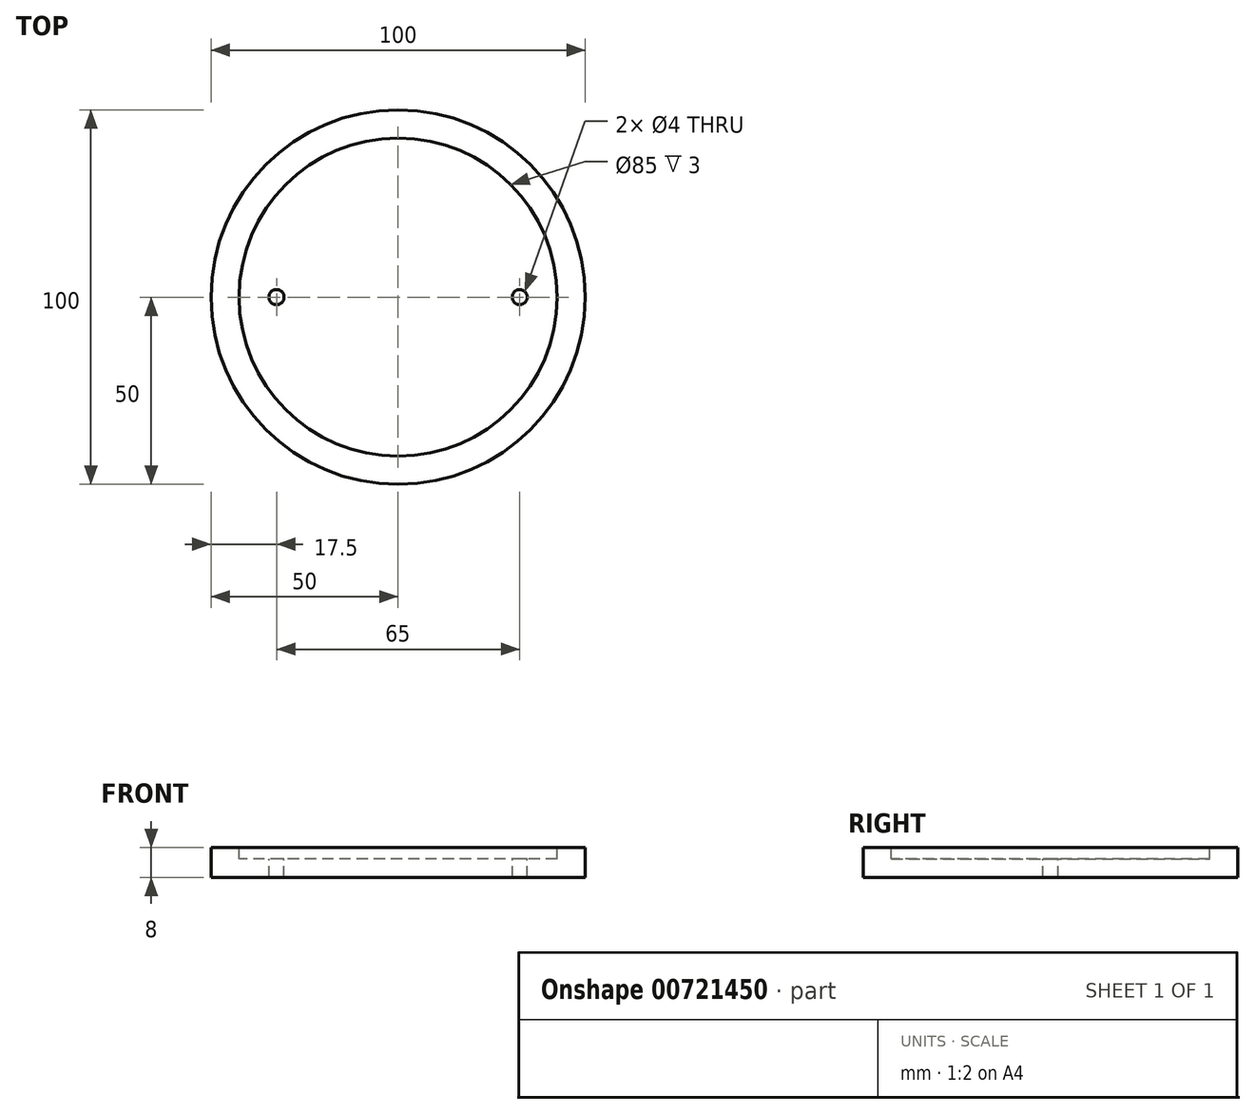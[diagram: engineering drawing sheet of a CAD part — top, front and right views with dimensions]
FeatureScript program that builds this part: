
annotation { "Feature Type Name" : "Feature", "Feature Type Description" : "" }
export const myFeature = defineFeature(function(context is Context, id is Id, definition is map)
    precondition{}
    {
        {
            var Q0;
            Q0=qCreatedBy(makeId("Top.planeOp"),FACE);
            var sketch = newSketch(context, id + "F0", { "sketchPlane" : qUnion([Q0])});
            skCircle(sketch, "E0", {"center": v(0, 0) * mm, "radius": 50 * mm});
            skSolve(sketch);
        }
        {
            var Q0;
            Q0 = qSketchRegion(id + "F0", true);
            extrude(context, id + "F1", {"entities" : qUnion([Q0]), "depth" : 8 * mm, "offsetDistance" : 25 * mm});
        }
        {
            var Q0;
            Q0=makeQuery(id+"F1.opExtrude","CAP_FACE",FACE,{"disambiguationData":[OSD([sQuery(id+"F0.wireOp",EDGE,"E0")])],"isStart":false});
            var sketch = newSketch(context, id + "F2", { "sketchPlane" : qUnion([Q0])});
            skCircle(sketch, "E1", {"center": v(0, 0) * mm, "radius": 42.5 * mm});
            skSolve(sketch);
        }
        {
            var Q0;
            Q0 = qSketchRegion(id + "F2", true);
            extrude(context, id + "F3", {"entities" : qUnion([Q0]), "operationType" : NewBodyOperationType.REMOVE, "oppositeDirection" : true, "depth" : 3 * mm, "offsetDistance" : 25 * mm});
        }
        {
            var Q0;
            Q0=makeQuery(id+"F3.boolean.opBoolean","COPY",FACE,{"derivedFrom":makeQuery(id+"F3.opExtrude","CAP_FACE",FACE,{"disambiguationData":[OSD([sQuery(id+"F2.wireOp",EDGE,"E1")])],"isStart":false})});
            var sketch = newSketch(context, id + "F4", { "sketchPlane" : qUnion([Q0])});
            skCircle(sketch, "E2", {"center": v(-32.5, 0) * mm, "radius": 2 * mm});
            skCircle(sketch, "E3.MirrorC", {"center": v(32.5, 0) * mm, "radius": 2 * mm});
            skSolve(sketch);
        }
        {
            var Q0;
            Q0 = qSketchRegion(id + "F4", true);
            extrude(context, id + "F5", {"entities" : qUnion([Q0]), "operationType" : NewBodyOperationType.REMOVE, "oppositeDirection" : true, "depth" : 25 * mm, "offsetDistance" : 25 * mm});
        }
    });
